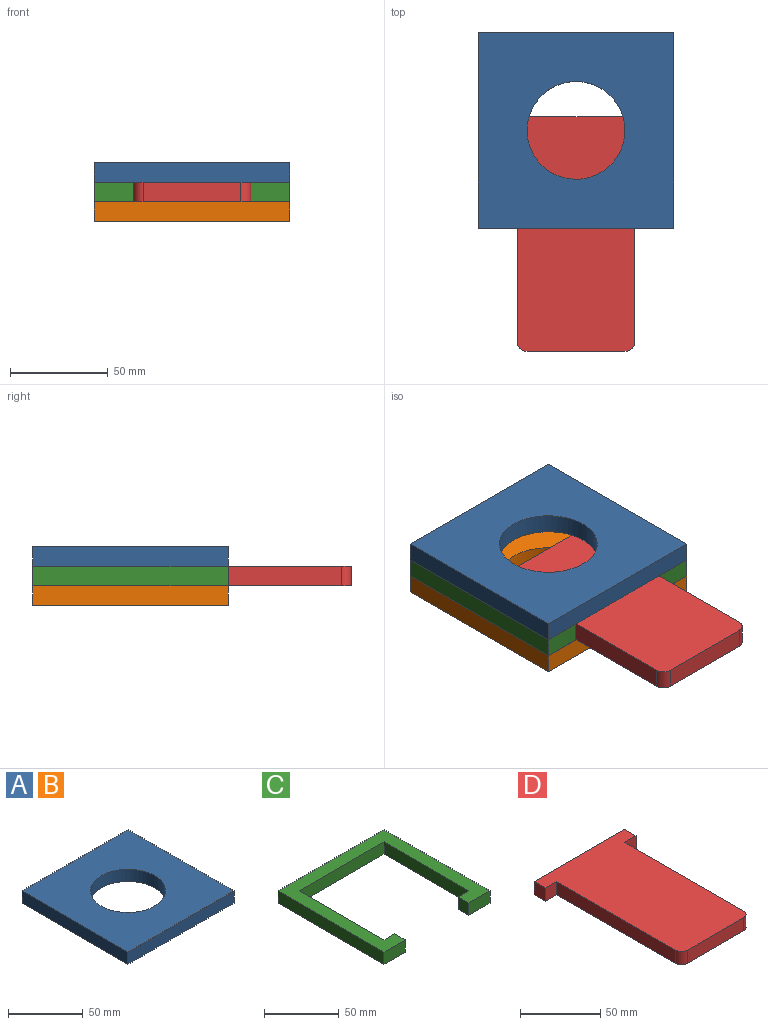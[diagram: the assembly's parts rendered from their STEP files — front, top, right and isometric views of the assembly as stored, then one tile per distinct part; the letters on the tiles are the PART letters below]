
ASSEMBLY  parts=4 mates=8
PART A: 7 faces, bbox 100x100x10 mm
  f0: plane 100x10mm, normal (1,0,0), area 1000mm2, adj f1,f3,f5,f6
  f1: plane 100x10mm, normal (0,1,0), area 1000mm2, adj f0,f2,f5,f6
  f2: plane 100x10mm, normal (-1,0,0), area 1000mm2, adj f1,f3,f5,f6
  f3: plane 100x10mm, normal (0,-1,0), area 1000mm2, adj f0,f2,f5,f6
  f4: cylinder r=25mm len=50mm, axis (0,0,-1), area 1570.8mm2, adj f5,f6
  f5: plane 100x100mm, normal (0,0,1), area 8036.5mm2, adj f0,f1,f2,f3,f4
  f6: plane 100x100mm, normal (0,0,-1), area 8036.5mm2, adj f0,f1,f2,f3,f4
PART B: same geometry as A
PART C: 14 faces, bbox 100x100x10 mm
  f0: plane 80x10mm, normal (-1,0,0), area 800mm2, adj f1,f11,f12,f13
  f1: plane 10x10mm, normal (0,1,0), area 100mm2, adj f0,f2,f12,f13
  f2: plane 10x10mm, normal (-1,0,0), area 100mm2, adj f1,f3,f12,f13
  f3: plane 20x10mm, normal (0,-1,0), area 200mm2, adj f2,f4,f12,f13
  f4: plane 100x10mm, normal (1,0,0), area 1000mm2, adj f3,f5,f12,f13
  f5: plane 100x10mm, normal (0,1,0), area 1000mm2, adj f4,f6,f12,f13
  f6: plane 100x10mm, normal (-1,0,0), area 1000mm2, adj f5,f7,f12,f13
  f7: plane 20x10mm, normal (0,-1,0), area 200mm2, adj f6,f8,f12,f13
  f8: plane 10x10mm, normal (1,0,0), area 100mm2, adj f7,f9,f12,f13
  f9: plane 10x10mm, normal (0,1,0), area 100mm2, adj f8,f10,f12,f13
  f10: plane 80x10mm, normal (1,0,0), area 800mm2, adj f9,f11,f12,f13
  f11: plane 80x10mm, normal (0,-1,0), area 800mm2, adj f0,f10,f12,f13
  f12: plane 100x100mm, normal (0,0,1), area 3000mm2, adj f0,f1,f2,f3,f4,f5,f6,f7
  f13: plane 100x100mm, normal (0,0,-1), area 3000mm2, adj f0,f1,f2,f3,f4,f5,f6,f7
PART D: 12 faces, bbox 80x120x10 mm
  f0: plane 10x10mm, normal (0,-1,0), area 100mm2, adj f1,f7,f8,f9
  f1: plane 105x10mm, normal (-1,0,0), area 1050mm2, adj f0,f8,f9,f10
  f2: plane 50x10mm, normal (0,-1,0), area 500mm2, adj f8,f9,f10,f11
  f3: plane 105x10mm, normal (1,0,0), area 1050mm2, adj f4,f8,f9,f11
  f4: plane 10x10mm, normal (0,-1,0), area 100mm2, adj f3,f5,f8,f9
  f5: plane 10x10mm, normal (1,0,0), area 100mm2, adj f4,f6,f8,f9
  f6: plane 80x10mm, normal (0,1,0), area 800mm2, adj f5,f7,f8,f9
  f7: plane 10x10mm, normal (-1,0,0), area 100mm2, adj f0,f6,f8,f9
  f8: plane 120x80mm, normal (0,0,1), area 7389.3mm2, adj f0,f1,f2,f3,f4,f5,f6,f7
  f9: plane 120x80mm, normal (0,0,-1), area 7389.3mm2, adj f0,f1,f2,f3,f4,f5,f6,f7
  f10: cylinder r=5mm len=10mm, axis (0,0,1), area 78.5mm2, adj f1,f2,f8,f9
  f11: cylinder r=5mm len=10mm, axis (0,0,-1), area 78.5mm2, adj f2,f3,f8,f9
PLACE A t=(0,0,20)mm
PLACE B at identity fixed
PLACE C t=(0,0,10)mm
PLACE D t=(0,-53.01,10)mm
MATE planar A.f0 <-> C.f4  axis (1,0,0) through (50,0,25)mm
MATE planar A.f3 <-> C.f3  axis (0,-1,0) through (0,-50,25)mm
MATE planar D.f3 <-> C.f2  axis (1,0,0) through (30,-55.51,15)mm
MATE planar C.f13 <-> B.f4  axis (0,0,-1) through (0,9,10)mm
MATE planar C.f4 <-> B.f0  axis (1,0,0) through (50,0,15)mm
MATE planar A.f4 <-> C.f12  axis (0,0,-1) through (0,0,20)mm
MATE planar D.f9 <-> B.f4  axis (0,0,-1) through (0,-51.44,10)mm
MATE planar C.f5 <-> B.f1  axis (0,1,0) through (0,50,15)mm
